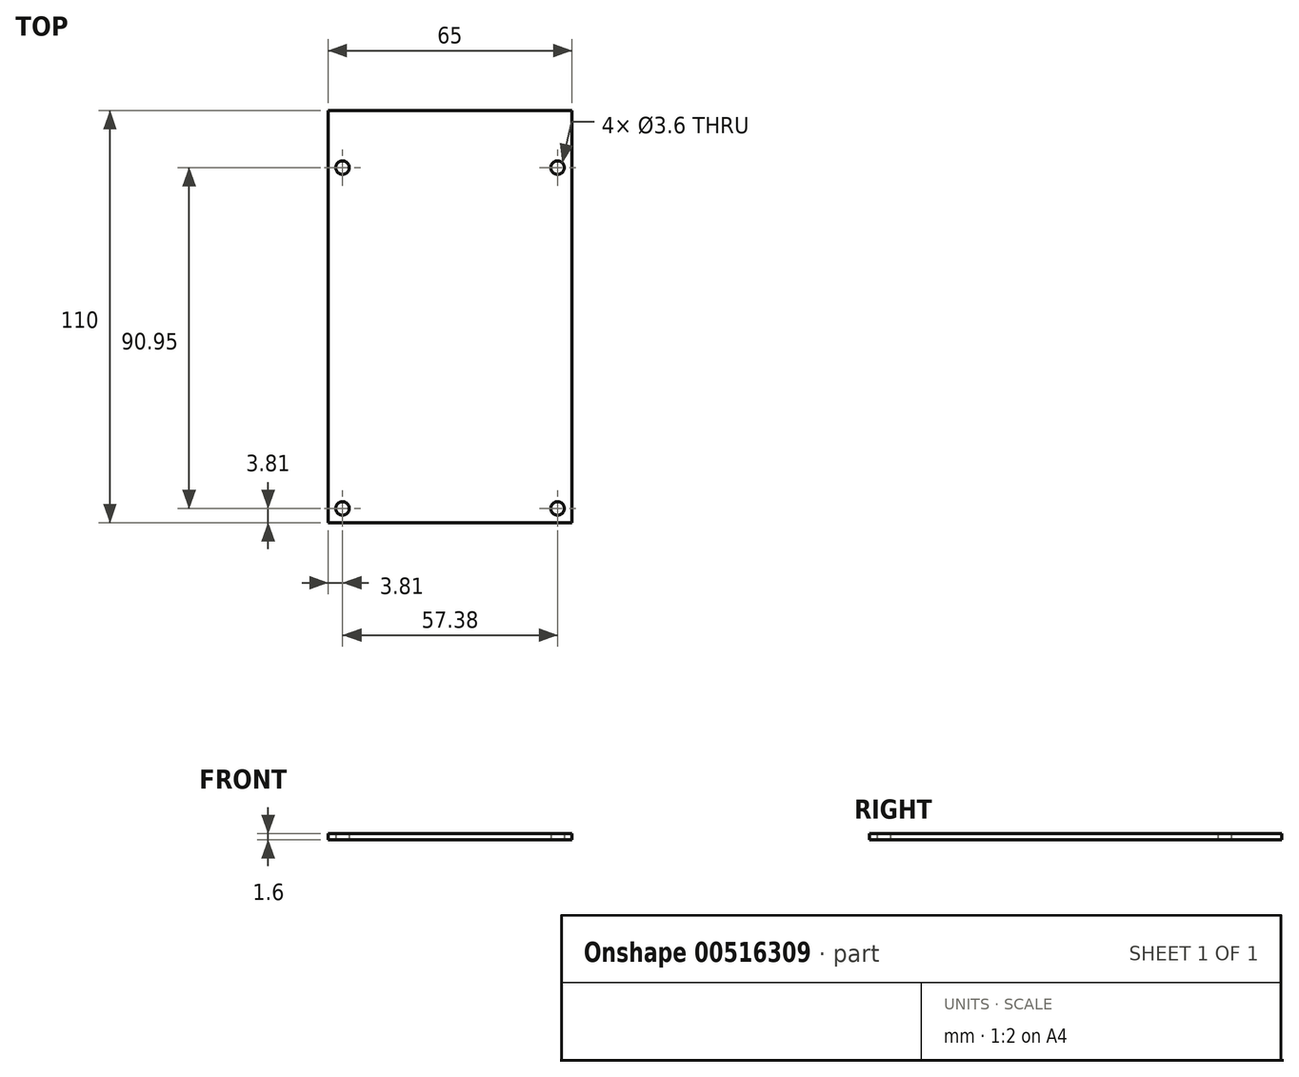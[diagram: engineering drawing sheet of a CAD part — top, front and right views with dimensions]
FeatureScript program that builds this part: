
annotation { "Feature Type Name" : "Feature", "Feature Type Description" : "" }
export const myFeature = defineFeature(function(context is Context, id is Id, definition is map)
    precondition{}
    {
        {
            var Q0;
            Q0=qCreatedBy(makeId("Top.planeOp"),FACE);
            var sketch = newSketch(context, id + "F0", { "sketchPlane" : qUnion([Q0])});
            skLineSegment(sketch, "E0.bottom", {"start": v(0, 0) * mm, "end": v(65, 0) * mm});
            skLineSegment(sketch, "E0.top", {"start": v(0, 110) * mm, "end": v(65, 110) * mm});
            skLineSegment(sketch, "E0.left", {"start": v(0, 0) * mm, "end": v(0, 110) * mm});
            skLineSegment(sketch, "E0.right", {"start": v(65, 0) * mm, "end": v(65, 110) * mm});
            skLineSegment(sketch, "E1.left", {"start": v(3.8, 94.76) * mm, "end": v(3.81, 3.81) * mm, "construction": true});
            skLineSegment(sketch, "E1.right", {"start": v(61.19, 94.76) * mm, "end": v(61.2, 3.81) * mm, "construction": true});
            skSolve(sketch);
        }
        {
            var Q0;
            Q0=makeQuery(id+"F0.imprint","IMPRINT",FACE,{"disambiguationData":[TD([[makeQuery(id+"F0.imprint","IMPRINT",EDGE,{"derivedFrom":sQuery(id+"F0.wireOp",EDGE,"E0.bottom")}),1.0]])]});
            extrude(context, id + "F1", {"entities" : qUnion([Q0]), "depth" : 1.6 * mm});
        }
        {
            var Q0;
            Q0=sQuery(id+"F0.wireOp",VERTEX,"E1.left.start");
            var Q1;
            Q1=sQuery(id+"F0.wireOp",VERTEX,"E1.right.start");
            var Q2;
            Q2=sQuery(id+"F0.wireOp",VERTEX,"E1.left.end");
            var Q3;
            Q3=sQuery(id+"F0.wireOp",VERTEX,"E1.right.end");
            var Q4;
            Q4=makeQuery(id+"F1.opExtrude","SWEPT_BODY",BODY,{"disambiguationData":[OSD([sQuery(id+"F0.wireOp",EDGE,"E0.bottom"),sQuery(id+"F0.wireOp",EDGE,"E0.top"),sQuery(id+"F0.wireOp",EDGE,"E0.left"),sQuery(id+"F0.wireOp",EDGE,"E0.right")])]});
            hole(context, id + "F2", {"style" : HoleStyle.SIMPLE, "endStyle" : HoleEndStyle.THROUGH, "oppositeDirection" : true, "holeDiameter" : 3.6 * mm, "isTappedThrough" : true, "tappedDepth" : 12 * mm, "tapClearance" : 3, "locations" : qUnion([Q0, Q1, Q2, Q3]), "scope" : qUnion([Q4])});
        }
    });
